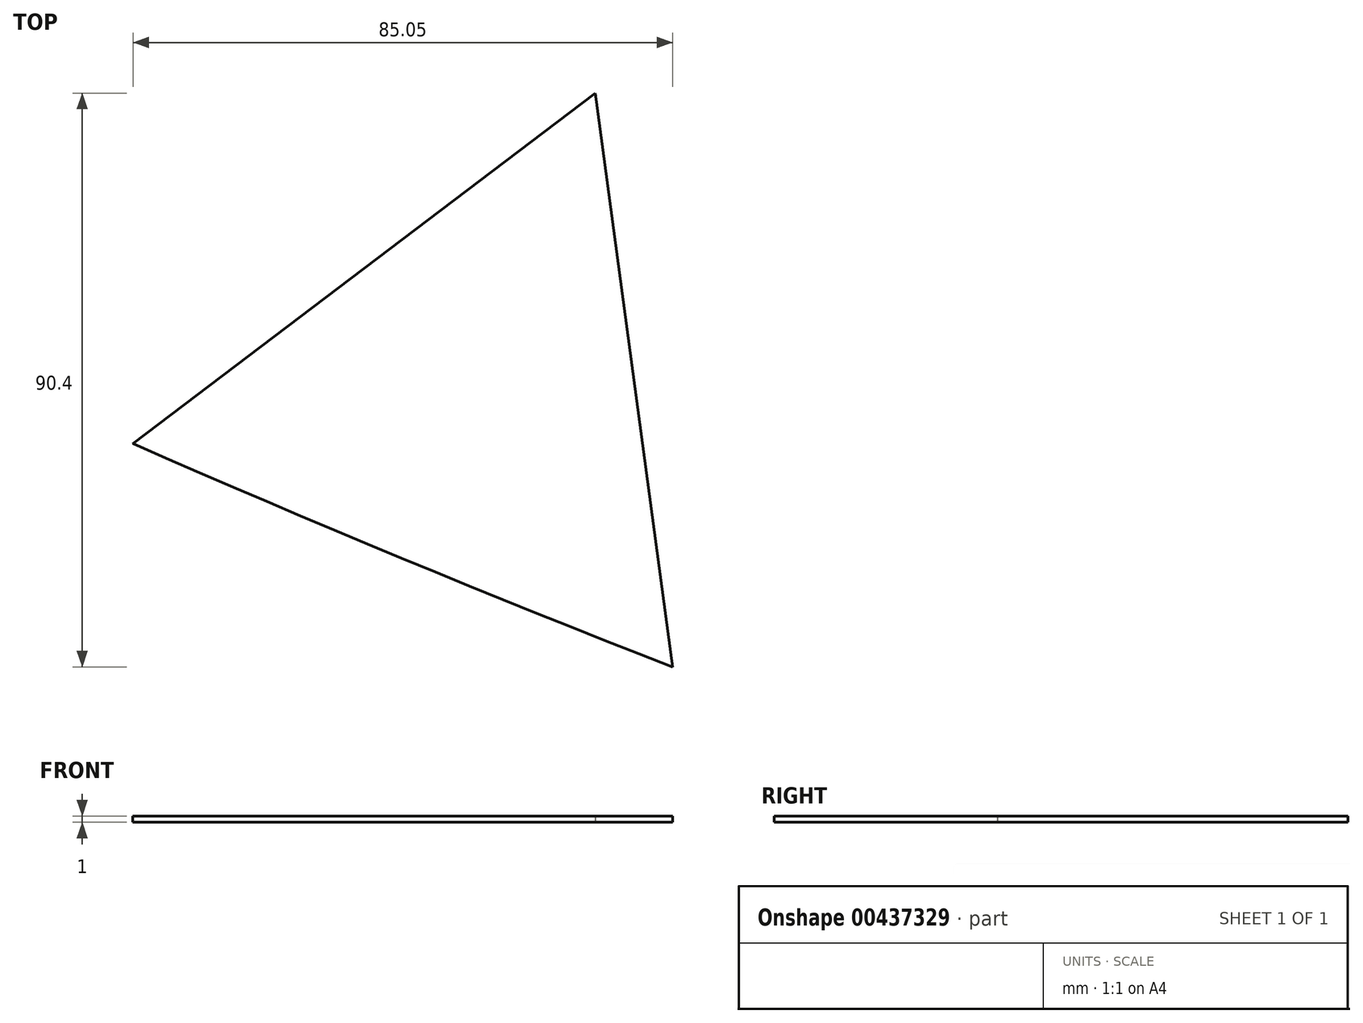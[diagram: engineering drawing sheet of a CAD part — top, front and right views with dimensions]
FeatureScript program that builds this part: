
annotation { "Feature Type Name" : "Feature", "Feature Type Description" : "" }
export const myFeature = defineFeature(function(context is Context, id is Id, definition is map)
    precondition{}
    {
        {
            var Q0;
            Q0=qCreatedBy(makeId("Top.planeOp"),FACE);
            var sketch = newSketch(context, id + "F0", { "sketchPlane" : qUnion([Q0])});
            skLineSegment(sketch, "E0", {"start": v(-45, 0) * mm, "end": v(27.88, 55.22) * mm});
            skLineSegment(sketch, "E1", {"start": v(27.88, 55.22) * mm, "end": v(40.06, -35.18) * mm});
            skArc(sketch, "E2", {"start": v(-45, 0) * mm, "mid": v(-2.66, -18.06) * mm, "end": v(40.06, -35.18) * mm});
            skSolve(sketch);
        }
        {
            var Q0;
            Q0=makeQuery(id+"F0.imprint","IMPRINT",FACE,{"disambiguationData":[TD([[makeQuery(id+"F0.imprint","IMPRINT",EDGE,{"derivedFrom":sQuery(id+"F0.wireOp",EDGE,"E0")}),-1.0]])]});
            extrude(context, id + "F1", {"entities" : qUnion([Q0]), "depth" : 1 * mm});
        }
    });
